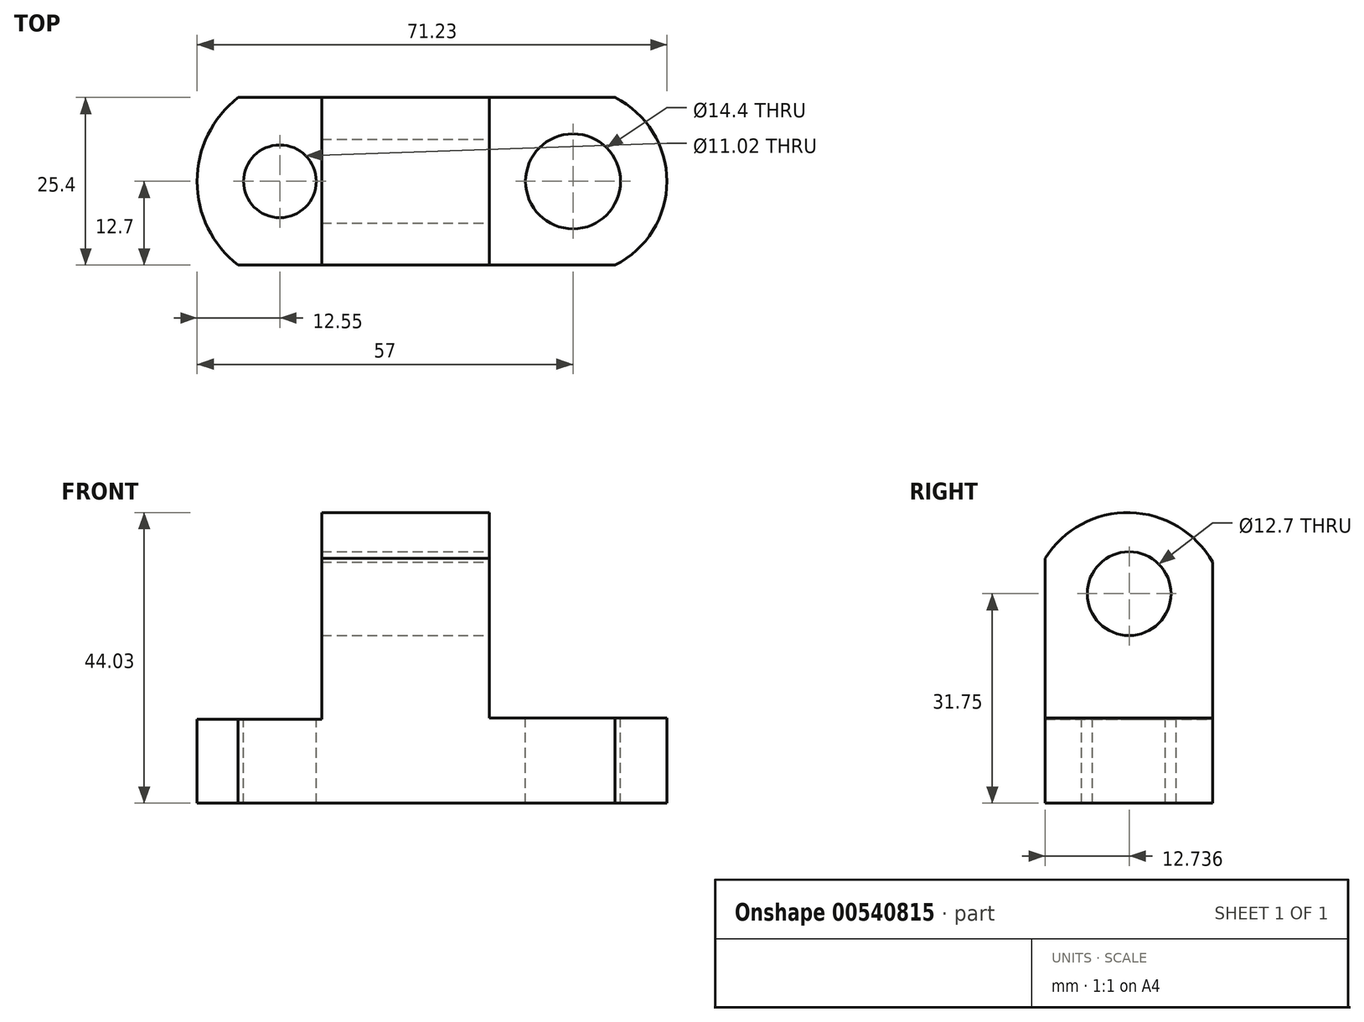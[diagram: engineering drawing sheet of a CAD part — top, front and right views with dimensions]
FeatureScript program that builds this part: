
annotation { "Feature Type Name" : "Feature", "Feature Type Description" : "" }
export const myFeature = defineFeature(function(context is Context, id is Id, definition is map)
    precondition{}
    {
        {
            var Q0;
            Q0=qCreatedBy(makeId("Front.planeOp"),FACE);
            var sketch = newSketch(context, id + "F0", { "sketchPlane" : qUnion([Q0])});
            skLineSegment(sketch, "E0", {"start": v(0, 0) * mm, "end": v(0, 12.7) * mm});
            skLineSegment(sketch, "E1", {"start": v(0, 12.7) * mm, "end": v(19.05, 12.7) * mm});
            skLineSegment(sketch, "E2", {"start": v(19.05, 12.7) * mm, "end": v(19.05, 44.45) * mm});
            skLineSegment(sketch, "E3", {"start": v(19.05, 44.45) * mm, "end": v(44.45, 44.45) * mm});
            skLineSegment(sketch, "E4", {"start": v(44.45, 44.45) * mm, "end": v(44.45, 12.91) * mm});
            skLineSegment(sketch, "E5", {"start": v(44.45, 12.91) * mm, "end": v(76.2, 12.91) * mm});
            skLineSegment(sketch, "E6", {"start": v(76.2, 12.91) * mm, "end": v(76.2, 0) * mm});
            skLineSegment(sketch, "E7", {"start": v(76.2, 0) * mm, "end": v(0, 0) * mm});
            skSolve(sketch);
        }
        {
            var Q0;
            Q0=makeQuery(id+"F0.imprint","IMPRINT",FACE,{"disambiguationData":[TD([[makeQuery(id+"F0.imprint","IMPRINT",EDGE,{"derivedFrom":sQuery(id+"F0.wireOp",EDGE,"E0")}),-1.0]])]});
            extrude(context, id + "F1", {"entities" : qUnion([Q0]), "depth" : 25.4 * mm, "offsetDistance" : 25.4 * mm});
        }
        {
            var Q0;
            Q0=makeQuery(id+"F1.opExtrude","SWEPT_FACE",FACE,{"disambiguationData":[OSD([sQuery(id+"F0.wireOp",EDGE,"E4")])]});
            var sketch = newSketch(context, id + "F2", { "sketchPlane" : qUnion([Q0])});
            skCircle(sketch, "E8", {"center": v(-12.66, 31.75) * mm, "radius": 6.35 * mm});
            skArc(sketch, "E9", {"start": v(0, 36.55) * mm, "mid": v(-12.54, 44.03) * mm, "end": v(-25.4, 37.13) * mm});
            skSolve(sketch);
        }
        {
            var Q0;
            {var subQ0=sQuery(id+"F2.wireOp",EDGE,"E9");Q0=makeQuery(id+"F2.imprint","IMPRINT",FACE,{"disambiguationData":[TD([[makeQuery(id+"F2.imprint","IMPRINT",EDGE,{"derivedFrom":subQ0}),-1.0]])]});}
            var Q1;
            Q1=makeQuery(id+"F2.imprint","IMPRINT",FACE,{"disambiguationData":[TD([[makeQuery(id+"F2.imprint","IMPRINT",EDGE,{"derivedFrom":sQuery(id+"F2.wireOp",EDGE,"E8")}),1.0]])]});
            extrude(context, id + "F3", {"entities" : qUnion([Q0, Q1]), "operationType" : NewBodyOperationType.REMOVE, "oppositeDirection" : true, "depth" : 25.4 * mm, "offsetDistance" : 25.4 * mm});
        }
        {
            var Q0;
            Q0=makeQuery(id+"F1.opExtrude","SWEPT_FACE",FACE,{"disambiguationData":[OSD([sQuery(id+"F0.wireOp",EDGE,"E5")])]});
            var sketch = newSketch(context, id + "F4", { "sketchPlane" : qUnion([Q0])});
            skCircle(sketch, "E10", {"center": v(57.15, -12.7) * mm, "radius": 7.2 * mm});
            skArc(sketch, "E11", {"start": v(63.5, -25.4) * mm, "mid": v(71.38, -12.7) * mm, "end": v(63.5, 0) * mm});
            skSolve(sketch);
        }
        {
            var Q0;
            Q0=makeQuery(id+"F4.imprint","IMPRINT",FACE,{"disambiguationData":[TD([[makeQuery(id+"F4.imprint","IMPRINT",EDGE,{"derivedFrom":sQuery(id+"F4.wireOp",EDGE,"E10")}),1.0]])]});
            var Q1;
            {var subQ0=sQuery(id+"F4.wireOp",EDGE,"E11");Q1=makeQuery(id+"F4.imprint","IMPRINT",FACE,{"disambiguationData":[TD([[makeQuery(id+"F4.imprint","IMPRINT",EDGE,{"derivedFrom":subQ0}),-1.0]])]});}
            extrude(context, id + "F5", {"entities" : qUnion([Q0, Q1]), "operationType" : NewBodyOperationType.REMOVE, "oppositeDirection" : true, "depth" : 25.4 * mm, "offsetDistance" : 25.4 * mm});
        }
        {
            var Q0;
            Q0=makeQuery(id+"F1.opExtrude","SWEPT_FACE",FACE,{"disambiguationData":[OSD([sQuery(id+"F0.wireOp",EDGE,"E1")])]});
            var sketch = newSketch(context, id + "F6", { "sketchPlane" : qUnion([Q0])});
            skCircle(sketch, "E12", {"center": v(12.7, -12.7) * mm, "radius": 5.51 * mm});
            skArc(sketch, "E13", {"start": v(6.35, 0) * mm, "mid": v(0.15, -12.7) * mm, "end": v(6.35, -25.4) * mm});
            skSolve(sketch);
        }
        {
            var Q0;
            {var subQ0=sQuery(id+"F6.wireOp",EDGE,"E13");Q0=makeQuery(id+"F6.imprint","IMPRINT",FACE,{"disambiguationData":[TD([[makeQuery(id+"F6.imprint","IMPRINT",EDGE,{"derivedFrom":subQ0}),-1.0]])]});}
            var Q1;
            Q1=makeQuery(id+"F6.imprint","IMPRINT",FACE,{"disambiguationData":[TD([[makeQuery(id+"F6.imprint","IMPRINT",EDGE,{"derivedFrom":sQuery(id+"F6.wireOp",EDGE,"E12")}),1.0]])]});
            extrude(context, id + "F7", {"entities" : qUnion([Q0, Q1]), "operationType" : NewBodyOperationType.REMOVE, "oppositeDirection" : true, "depth" : 25.4 * mm, "offsetDistance" : 25.4 * mm});
        }
    });
